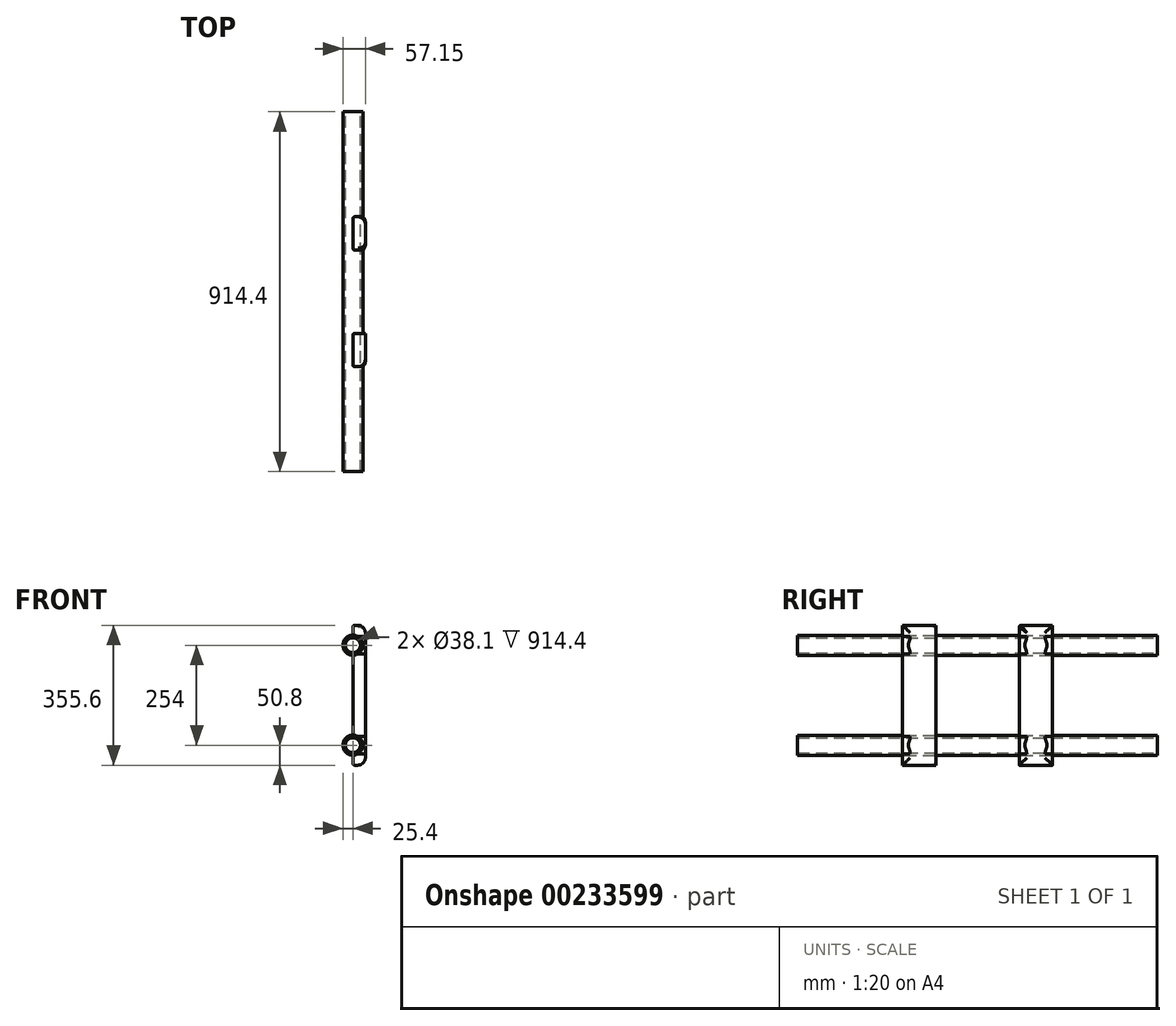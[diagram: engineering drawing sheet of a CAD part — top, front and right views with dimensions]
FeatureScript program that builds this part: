
annotation { "Feature Type Name" : "Feature", "Feature Type Description" : "" }
export const myFeature = defineFeature(function(context is Context, id is Id, definition is map)
    precondition{}
    {
        {
            var Q0;
            Q0=qCreatedBy(makeId("Front.planeOp"),FACE);
            var sketch = newSketch(context, id + "F0", { "sketchPlane" : qUnion([Q0])});
            skLineSegment(sketch, "E0", {"start": v(0, 0) * mm, "end": v(0, 76.2) * mm, "construction": true});
            skLineSegment(sketch, "E1", {"start": v(0, 76.2) * mm, "end": v(0, 0) * mm, "construction": true});
            skLineSegment(sketch, "E2", {"start": v(0, 0) * mm, "end": v(0, -76.2) * mm, "construction": true});
            skCircle(sketch, "E3", {"center": v(0, -76.2) * mm, "radius": 25.4 * mm});
            skCircle(sketch, "E4", {"center": v(0, -76.2) * mm, "radius": 19.05 * mm});
            skLineSegment(sketch, "E5", {"start": v(0, 101.6) * mm, "end": v(0, 127) * mm});
            skLineSegment(sketch, "E6", {"start": v(0, -101.6) * mm, "end": v(0, -127) * mm});
            skLineSegment(sketch, "E7", {"start": v(0, -127) * mm, "end": v(31.75, -127) * mm});
            skLineSegment(sketch, "E8", {"start": v(31.75, -127) * mm, "end": v(31.75, 127) * mm});
            skLineSegment(sketch, "E9", {"start": v(0, 50.8) * mm, "end": v(0, -50.8) * mm});
            skLineSegment(sketch, "E10", {"start": v(0, 0) * mm, "end": v(0, 177.8) * mm});
            skCircle(sketch, "E11", {"center": v(0, 177.8) * mm, "radius": 25.4 * mm});
            skCircle(sketch, "E12", {"center": v(0, 177.8) * mm, "radius": 19.05 * mm});
            skLineSegment(sketch, "E13", {"start": v(0, 203.2) * mm, "end": v(0, 228.6) * mm});
            skLineSegment(sketch, "E14", {"start": v(0, 228.6) * mm, "end": v(31.75, 228.6) * mm});
            skLineSegment(sketch, "E15", {"start": v(31.75, 228.6) * mm, "end": v(31.75, 127) * mm});
            skSolve(sketch);
        }
        {
            var Q0;
            {var subQ0=sQuery(id+"F0.wireOp",EDGE,"E6");Q0=makeQuery(id+"F0.imprint","IMPRINT",FACE,{"disambiguationData":[TD([[makeQuery(id+"F0.imprint","IMPRINT",EDGE,{"derivedFrom":subQ0}),1.0]])]});}
            extrude(context, id + "F1", {"entities" : qUnion([Q0]), "endBound" : BoundingType.SYMMETRIC, "depth" : 381 * mm});
        }
        {
            var Q0;
            Q0=makeQuery(id+"F1.opExtrude","SWEPT_FACE",FACE,{"disambiguationData":[OSD([sQuery(id+"F0.wireOp",EDGE,"E8"),sQuery(id+"F0.wireOp",EDGE,"E15")])]});
            var sketch = newSketch(context, id + "F2", { "sketchPlane" : qUnion([Q0])});
            skLineSegment(sketch, "E16.bottom", {"start": v(105.61, -155.17) * mm, "end": v(-105.61, -155.17) * mm});
            skLineSegment(sketch, "E16.top", {"start": v(105.61, 256.77) * mm, "end": v(-105.61, 256.77) * mm});
            skLineSegment(sketch, "E16.left", {"start": v(105.61, -155.17) * mm, "end": v(105.61, 256.77) * mm});
            skLineSegment(sketch, "E16.right", {"start": v(-105.61, -155.17) * mm, "end": v(-105.61, 256.77) * mm});
            skPoint(sketch, "E16.middle", {"position": v(0, 50.8) * mm});
            skPoint(sketch, "E16.middle.positionSnap0", {"position": v(-190.5, 50.8) * mm});
            skPoint(sketch, "E16.middle.positionSnap1", {"position": v(0, 228.6) * mm});
            skPoint(sketch, "E16.centerSnap0", {"position": v(-190.5, 50.8) * mm});
            skPoint(sketch, "E16.centerSnap1", {"position": v(0, 228.6) * mm});
            skSolve(sketch);
        }
        {
            var Q0;
            Q0=qSketchRegion(id+"F2",true);
            extrude(context, id + "F3", {"entities" : qUnion([Q0]), "operationType" : NewBodyOperationType.REMOVE, "endBound" : BoundingType.THROUGH_ALL, "oppositeDirection" : true, "depth" : 25.4 * mm});
        }
        {
            var Q0;
            Q0=makeQuery(id+"F0.imprint","IMPRINT",FACE,{"disambiguationData":[TD([[makeQuery(id+"F0.imprint","IMPRINT",EDGE,{"derivedFrom":sQuery(id+"F0.wireOp",EDGE,"E12")}),-1.0]])]});
            extrude(context, id + "F4", {"entities" : qUnion([Q0]), "depth" : 25.4 * mm});
        }
        {
            var Q0;
            Q0=makeQuery(id+"F0.imprint","IMPRINT",FACE,{"disambiguationData":[TD([[makeQuery(id+"F0.imprint","IMPRINT",EDGE,{"derivedFrom":sQuery(id+"F0.wireOp",EDGE,"E4")}),-1.0]])]});
            var Q1;
            Q1=makeQuery(id+"F0.imprint","IMPRINT",FACE,{"disambiguationData":[TD([[makeQuery(id+"F0.imprint","IMPRINT",EDGE,{"derivedFrom":sQuery(id+"F0.wireOp",EDGE,"E12")}),-1.0]])]});
            extrude(context, id + "F5", {"entities" : qUnion([Q0, Q1]), "operationType" : NewBodyOperationType.ADD, "endBound" : BoundingType.SYMMETRIC, "depth" : 914.4 * mm});
        }
        {
            var Q0;
            Q0=makeQuery(id+"F1.opExtrude","CAP_EDGE",EDGE,{"disambiguationData":[OSD([sQuery(id+"F0.wireOp",EDGE,"E8"),sQuery(id+"F0.wireOp",EDGE,"E15")])],"isStart":false});
            var Q1;
            Q1=makeQuery(id+"F3.boolean.opBoolean","COPY",EDGE,{"derivedFrom":makeQuery(id+"F3.opExtrude","CAP_EDGE",EDGE,{"disambiguationData":[OSD([sQuery(id+"F2.wireOp",EDGE,"E16.right")])],"isStart":true})});
            var Q2;
            Q2=makeQuery(id+"F3.boolean.opBoolean","COPY",EDGE,{"derivedFrom":makeQuery(id+"F3.opExtrude","CAP_EDGE",EDGE,{"disambiguationData":[OSD([sQuery(id+"F2.wireOp",EDGE,"E16.left")])],"isStart":true})});
            var Q3;
            Q3=makeQuery(id+"F1.opExtrude","CAP_EDGE",EDGE,{"disambiguationData":[OSD([sQuery(id+"F0.wireOp",EDGE,"E8"),sQuery(id+"F0.wireOp",EDGE,"E15")])],"isStart":true});
            var Q4;
            {var subQ0=sQuery(id+"F0.wireOp",EDGE,"E15");var subQ1=sQuery(id+"F0.wireOp",EDGE,"E14");Q4=makeQuery(id+"F3.boolean.opBoolean","SPLIT",EDGE,{"disambiguationData":[TD([makeQuery(id+"F3.opExtrude","SWEPT_FACE",FACE,{"disambiguationData":[OSD([sQuery(id+"F2.wireOp",EDGE,"E16.right")])]})])],"derivedFrom":makeQuery(id+"F1.opExtrude","SWEPT_EDGE",EDGE,{"disambiguationData":[OSD([subQ1,subQ0])]})});}
            var Q5;
            {var subQ0=sQuery(id+"F0.wireOp",EDGE,"E15");var subQ1=sQuery(id+"F0.wireOp",EDGE,"E14");Q5=makeQuery(id+"F3.boolean.opBoolean","SPLIT",EDGE,{"disambiguationData":[TD([makeQuery(id+"F3.opExtrude","SWEPT_FACE",FACE,{"disambiguationData":[OSD([sQuery(id+"F2.wireOp",EDGE,"E16.left")])]})])],"derivedFrom":makeQuery(id+"F1.opExtrude","SWEPT_EDGE",EDGE,{"disambiguationData":[OSD([subQ1,subQ0])]})});}
            var Q6;
            {var subQ1=sQuery(id+"F0.wireOp",EDGE,"E8");var subQ2=sQuery(id+"F0.wireOp",EDGE,"E7");Q6=makeQuery(id+"F3.boolean.opBoolean","SPLIT",EDGE,{"disambiguationData":[TD([makeQuery(id+"F3.opExtrude","SWEPT_FACE",FACE,{"disambiguationData":[OSD([sQuery(id+"F2.wireOp",EDGE,"E16.left")])]})])],"derivedFrom":makeQuery(id+"F1.opExtrude","SWEPT_EDGE",EDGE,{"disambiguationData":[OSD([subQ2,subQ1])]})});}
            var Q7;
            {var subQ1=sQuery(id+"F0.wireOp",EDGE,"E8");var subQ2=sQuery(id+"F0.wireOp",EDGE,"E7");Q7=makeQuery(id+"F3.boolean.opBoolean","SPLIT",EDGE,{"disambiguationData":[TD([makeQuery(id+"F3.opExtrude","SWEPT_FACE",FACE,{"disambiguationData":[OSD([sQuery(id+"F2.wireOp",EDGE,"E16.right")])]})])],"derivedFrom":makeQuery(id+"F1.opExtrude","SWEPT_EDGE",EDGE,{"disambiguationData":[OSD([subQ2,subQ1])]})});}
            fillet(context, id + "F6", {"entities" : qUnion([Q0, Q1, Q2, Q3, Q4, Q5, Q6, Q7]), "radius" : 19.05 * mm, "tangentPropagation" : true, "allowEdgeOverflow" : false});
        }
        {
            var Q0;
            Q0=makeQuery(id+"F3.boolean.opBoolean","INTERSECT",EDGE,{"derivedFrom":[makeQuery(id+"F1.opExtrude","SWEPT_FACE",FACE,{"disambiguationData":[OSD([sQuery(id+"F0.wireOp",EDGE,"E9"),sQuery(id+"F0.wireOp",EDGE,"E10")])]}),makeQuery(id+"F3.opExtrude","SWEPT_FACE",FACE,{"disambiguationData":[OSD([sQuery(id+"F2.wireOp",EDGE,"E16.left")])]})]});
            var Q1;
            Q1=makeQuery(id+"F1.opExtrude","CAP_EDGE",EDGE,{"disambiguationData":[OSD([sQuery(id+"F0.wireOp",EDGE,"E9"),sQuery(id+"F0.wireOp",EDGE,"E10")])],"isStart":false});
            var Q2;
            Q2=makeQuery(id+"F1.opExtrude","CAP_EDGE",EDGE,{"disambiguationData":[OSD([sQuery(id+"F0.wireOp",EDGE,"E13")])],"isStart":false});
            var Q3;
            {var subQ0=sQuery(id+"F0.wireOp",EDGE,"E14");var subQ1=sQuery(id+"F0.wireOp",EDGE,"E13");Q3=makeQuery(id+"F3.boolean.opBoolean","SPLIT",EDGE,{"disambiguationData":[TD([makeQuery(id+"F3.opExtrude","SWEPT_FACE",FACE,{"disambiguationData":[OSD([sQuery(id+"F2.wireOp",EDGE,"E16.right")])]})])],"derivedFrom":makeQuery(id+"F1.opExtrude","SWEPT_EDGE",EDGE,{"disambiguationData":[OSD([subQ1,subQ0])]})});}
            var Q4;
            Q4=makeQuery(id+"F3.boolean.opBoolean","INTERSECT",EDGE,{"derivedFrom":[makeQuery(id+"F1.opExtrude","SWEPT_FACE",FACE,{"disambiguationData":[OSD([sQuery(id+"F0.wireOp",EDGE,"E13")])]}),makeQuery(id+"F3.opExtrude","SWEPT_FACE",FACE,{"disambiguationData":[OSD([sQuery(id+"F2.wireOp",EDGE,"E16.right")])]})]});
            var Q5;
            Q5=makeQuery(id+"F3.boolean.opBoolean","INTERSECT",EDGE,{"derivedFrom":[makeQuery(id+"F1.opExtrude","SWEPT_FACE",FACE,{"disambiguationData":[OSD([sQuery(id+"F0.wireOp",EDGE,"E9"),sQuery(id+"F0.wireOp",EDGE,"E10")])]}),makeQuery(id+"F3.opExtrude","SWEPT_FACE",FACE,{"disambiguationData":[OSD([sQuery(id+"F2.wireOp",EDGE,"E16.right")])]})]});
            var Q6;
            Q6=makeQuery(id+"F3.boolean.opBoolean","INTERSECT",EDGE,{"derivedFrom":[makeQuery(id+"F1.opExtrude","SWEPT_FACE",FACE,{"disambiguationData":[OSD([sQuery(id+"F0.wireOp",EDGE,"E6")])]}),makeQuery(id+"F3.opExtrude","SWEPT_FACE",FACE,{"disambiguationData":[OSD([sQuery(id+"F2.wireOp",EDGE,"E16.right")])]})]});
            var Q7;
            {var subQ0=sQuery(id+"F0.wireOp",EDGE,"E7");var subQ1=sQuery(id+"F0.wireOp",EDGE,"E6");Q7=makeQuery(id+"F3.boolean.opBoolean","SPLIT",EDGE,{"disambiguationData":[TD([makeQuery(id+"F3.opExtrude","SWEPT_FACE",FACE,{"disambiguationData":[OSD([sQuery(id+"F2.wireOp",EDGE,"E16.right")])]})])],"derivedFrom":makeQuery(id+"F1.opExtrude","SWEPT_EDGE",EDGE,{"disambiguationData":[OSD([subQ1,subQ0])]})});}
            var Q8;
            Q8=makeQuery(id+"F1.opExtrude","CAP_EDGE",EDGE,{"disambiguationData":[OSD([sQuery(id+"F0.wireOp",EDGE,"E6")])],"isStart":false});
            var Q9;
            Q9=makeQuery(id+"F3.boolean.opBoolean","INTERSECT",EDGE,{"derivedFrom":[makeQuery(id+"F1.opExtrude","SWEPT_FACE",FACE,{"disambiguationData":[OSD([sQuery(id+"F0.wireOp",EDGE,"E6")])]}),makeQuery(id+"F3.opExtrude","SWEPT_FACE",FACE,{"disambiguationData":[OSD([sQuery(id+"F2.wireOp",EDGE,"E16.left")])]})]});
            var Q10;
            Q10=makeQuery(id+"F1.opExtrude","CAP_EDGE",EDGE,{"disambiguationData":[OSD([sQuery(id+"F0.wireOp",EDGE,"E9"),sQuery(id+"F0.wireOp",EDGE,"E10")])],"isStart":true});
            var Q11;
            Q11=makeQuery(id+"F1.opExtrude","CAP_EDGE",EDGE,{"disambiguationData":[OSD([sQuery(id+"F0.wireOp",EDGE,"E6")])],"isStart":true});
            var Q12;
            {var subQ0=sQuery(id+"F0.wireOp",EDGE,"E7");var subQ1=sQuery(id+"F0.wireOp",EDGE,"E6");Q12=makeQuery(id+"F3.boolean.opBoolean","SPLIT",EDGE,{"disambiguationData":[TD([makeQuery(id+"F3.opExtrude","SWEPT_FACE",FACE,{"disambiguationData":[OSD([sQuery(id+"F2.wireOp",EDGE,"E16.left")])]})])],"derivedFrom":makeQuery(id+"F1.opExtrude","SWEPT_EDGE",EDGE,{"disambiguationData":[OSD([subQ1,subQ0])]})});}
            var Q13;
            Q13=makeQuery(id+"F3.boolean.opBoolean","INTERSECT",EDGE,{"derivedFrom":[makeQuery(id+"F1.opExtrude","SWEPT_FACE",FACE,{"disambiguationData":[OSD([sQuery(id+"F0.wireOp",EDGE,"E13")])]}),makeQuery(id+"F3.opExtrude","SWEPT_FACE",FACE,{"disambiguationData":[OSD([sQuery(id+"F2.wireOp",EDGE,"E16.left")])]})]});
            var Q14;
            {var subQ0=sQuery(id+"F0.wireOp",EDGE,"E14");var subQ1=sQuery(id+"F0.wireOp",EDGE,"E13");Q14=makeQuery(id+"F3.boolean.opBoolean","SPLIT",EDGE,{"disambiguationData":[TD([makeQuery(id+"F3.opExtrude","SWEPT_FACE",FACE,{"disambiguationData":[OSD([sQuery(id+"F2.wireOp",EDGE,"E16.left")])]})])],"derivedFrom":makeQuery(id+"F1.opExtrude","SWEPT_EDGE",EDGE,{"disambiguationData":[OSD([subQ1,subQ0])]})});}
            var Q15;
            Q15=makeQuery(id+"F3.boolean.opBoolean","INTERSECT",EDGE,{"derivedFrom":[makeQuery(id+"F1.opExtrude","SWEPT_FACE",FACE,{"disambiguationData":[OSD([sQuery(id+"F0.wireOp",EDGE,"E14")])]}),makeQuery(id+"F3.opExtrude","SWEPT_FACE",FACE,{"disambiguationData":[OSD([sQuery(id+"F2.wireOp",EDGE,"E16.left")])]})]});
            var Q16;
            Q16=makeQuery(id+"F1.opExtrude","CAP_EDGE",EDGE,{"disambiguationData":[OSD([sQuery(id+"F0.wireOp",EDGE,"E13")])],"isStart":true});
            fillet(context, id + "F7", {"entities" : qUnion([Q0, Q1, Q2, Q3, Q4, Q5, Q6, Q7, Q8, Q9, Q10, Q11, Q12, Q13, Q14, Q15, Q16]), "radius" : 5.08 * mm, "tangentPropagation" : true, "allowEdgeOverflow" : false});
        }
    });
